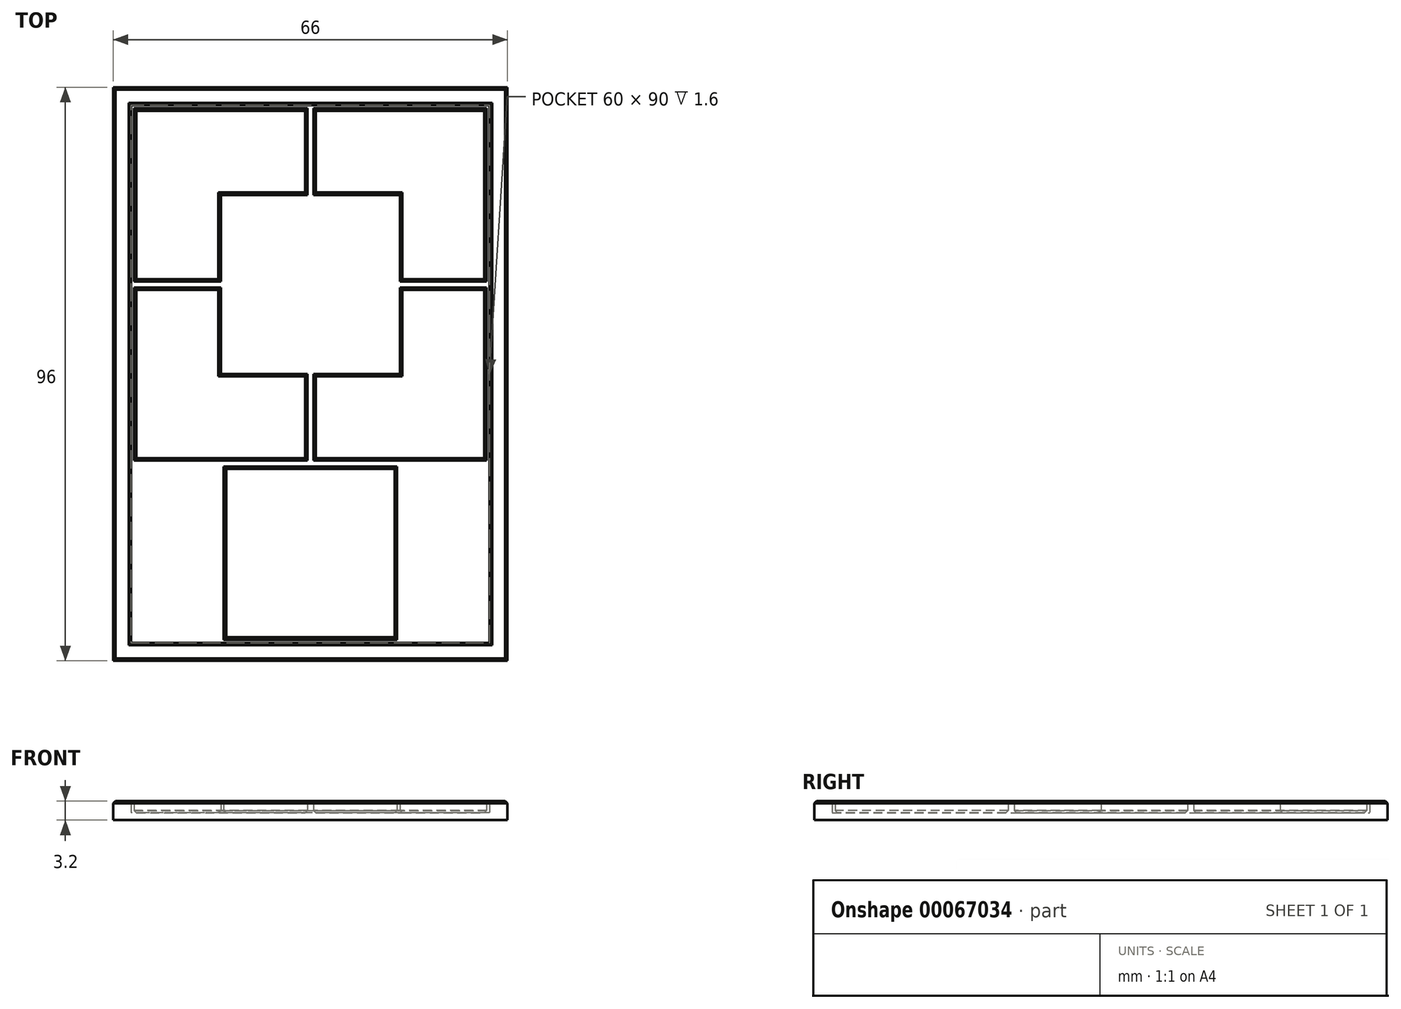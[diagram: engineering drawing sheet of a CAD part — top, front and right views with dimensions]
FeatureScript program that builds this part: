
annotation { "Feature Type Name" : "Feature", "Feature Type Description" : "" }
export const myFeature = defineFeature(function(context is Context, id is Id, definition is map)
    precondition{}
    {
        {
            var Q0;
            Q0=qCreatedBy(makeId("Top.planeOp"),FACE);
            var sketch = newSketch(context, id + "F0", { "sketchPlane" : qUnion([Q0])});
            skLineSegment(sketch, "E0.rect.bottom", {"start": v(-30, 45) * mm, "end": v(30, 45) * mm});
            skLineSegment(sketch, "E0.rect.top", {"start": v(-30, -45) * mm, "end": v(30, -45) * mm});
            skLineSegment(sketch, "E0.rect.left", {"start": v(-30, 45) * mm, "end": v(-30, -45) * mm});
            skLineSegment(sketch, "E0.rect.right", {"start": v(30, 45) * mm, "end": v(30, -45) * mm});
            skPoint(sketch, "E0.rect.middle", {"position": v(0, 0) * mm});
            skLineSegment(sketch, "E1.0", {"start": v(-33, 48) * mm, "end": v(-33, -48) * mm});
            skLineSegment(sketch, "E1.1", {"start": v(-33, 48) * mm, "end": v(33, 48) * mm});
            skLineSegment(sketch, "E1.2", {"start": v(33, 48) * mm, "end": v(33, -48) * mm});
            skLineSegment(sketch, "E1.3", {"start": v(-33, -48) * mm, "end": v(33, -48) * mm});
            skSolve(sketch);
        }
        {
            var Q0;
            Q0 = qSketchRegion(id + "F0", true);
            var Q1;
            Q1=makeQuery(id+"F0.imprint","IMPRINT",FACE,{"disambiguationData":[TD([[makeQuery(id+"F0.imprint","IMPRINT",EDGE,{"derivedFrom":sQuery(id+"F0.wireOp",EDGE,"E0.rect.bottom")}),-1.0]])]});
            extrude(context, id + "F1", {"entities" : qUnion([Q0, Q1]), "depth" : 1.2 * mm});
        }
        {
            var Q0;
            Q0=makeQuery(id+"F0.imprint","IMPRINT",FACE,{"disambiguationData":[TD([[makeQuery(id+"F0.imprint","IMPRINT",EDGE,{"derivedFrom":sQuery(id+"F0.wireOp",EDGE,"E0.rect.bottom")}),1.0]])]});
            extrude(context, id + "F2", {"entities" : qUnion([Q0]), "operationType" : NewBodyOperationType.ADD, "depth" : (1.2 + 2) * mm});
        }
        {
            var Q0;
            Q0=makeQuery(id+"F1.opExtrude","CAP_FACE",FACE,{"disambiguationData":[OSD([sQuery(id+"F0.wireOp",EDGE,"E1.0"),sQuery(id+"F0.wireOp",EDGE,"E1.1"),sQuery(id+"F0.wireOp",EDGE,"E1.2"),sQuery(id+"F0.wireOp",EDGE,"E1.3")])],"isStart":false});
            var sketch = newSketch(context, id + "F3", { "sketchPlane" : qUnion([Q0])});
            skLineSegment(sketch, "E2.bottom", {"start": v(-29.5, 44.5) * mm, "end": v(-0.5, 44.5) * mm});
            skLineSegment(sketch, "E2.top", {"start": v(-29.5, 15.5) * mm, "end": v(-15, 15.5) * mm});
            skLineSegment(sketch, "E2.left", {"start": v(-29.5, 44.5) * mm, "end": v(-29.5, 15.5) * mm});
            skLineSegment(sketch, "E2.right", {"start": v(-0.5, 44.5) * mm, "end": v(-0.5, 30) * mm});
            skLineSegment(sketch, "E3", {"start": v(-0.5, 30) * mm, "end": v(-15, 30) * mm});
            skLineSegment(sketch, "E4", {"start": v(-15, 30) * mm, "end": v(-15, 15.5) * mm});
            skLineSegment(sketch, "E5.0", {"start": v(-30, 45) * mm, "end": v(-30, -45) * mm, "construction": true});
            skLineSegment(sketch, "E5.1", {"start": v(-30, 45) * mm, "end": v(30, 45) * mm, "construction": true});
            skLineSegment(sketch, "E5.2", {"start": v(30, 45) * mm, "end": v(30, -45) * mm, "construction": true});
            skLineSegment(sketch, "E5.3", {"start": v(-30, -45) * mm, "end": v(30, -45) * mm, "construction": true});
            skLineSegment(sketch, "E6.0", {"start": v(-29.5, 44.5) * mm, "end": v(-29.5, -44.5) * mm, "construction": true});
            skLineSegment(sketch, "E6.1", {"start": v(-29.5, 44.5) * mm, "end": v(29.5, 44.5) * mm, "construction": true});
            skLineSegment(sketch, "E6.2", {"start": v(29.5, 44.5) * mm, "end": v(29.5, -44.5) * mm, "construction": true});
            skLineSegment(sketch, "E6.3", {"start": v(-29.5, -44.5) * mm, "end": v(29.5, -44.5) * mm, "construction": true});
            skLineSegment(sketch, "E7", {"start": v(-27.64, 15) * mm, "end": v(26.14, 15) * mm, "construction": true});
            skLineSegment(sketch, "E8", {"start": v(-27.76, -15) * mm, "end": v(23, -15) * mm, "construction": true});
            skLineSegment(sketch, "E9", {"start": v(0, -31.54) * mm, "end": v(0, 35.9) * mm, "construction": true});
            skLineSegment(sketch, "E10.1.0", {"start": v(-29.5, -14.5) * mm, "end": v(-0.5, -14.5) * mm});
            skLineSegment(sketch, "E10.1.1", {"start": v(-29.5, -14.5) * mm, "end": v(-29.5, 14.5) * mm});
            skLineSegment(sketch, "E10.1.2", {"start": v(-29.5, 14.5) * mm, "end": v(-15, 14.5) * mm});
            skLineSegment(sketch, "E10.1.3", {"start": v(-15, 14.5) * mm, "end": v(-15, 0) * mm});
            skLineSegment(sketch, "E10.1.4", {"start": v(-15, 0) * mm, "end": v(-0.5, 0) * mm});
            skLineSegment(sketch, "E10.1.5", {"start": v(-0.5, -14.5) * mm, "end": v(-0.5, 0) * mm});
            skLineSegment(sketch, "E10.2.0", {"start": v(29.5, -14.5) * mm, "end": v(29.5, 14.5) * mm});
            skLineSegment(sketch, "E10.2.1", {"start": v(29.5, -14.5) * mm, "end": v(0.5, -14.5) * mm});
            skLineSegment(sketch, "E10.2.2", {"start": v(0.5, -14.5) * mm, "end": v(0.5, 0) * mm});
            skLineSegment(sketch, "E10.2.3", {"start": v(0.5, 0) * mm, "end": v(15, 0) * mm});
            skLineSegment(sketch, "E10.2.4", {"start": v(15, 0) * mm, "end": v(15, 14.5) * mm});
            skLineSegment(sketch, "E10.2.5", {"start": v(29.5, 14.5) * mm, "end": v(15, 14.5) * mm});
            skLineSegment(sketch, "E10.3.0", {"start": v(29.5, 44.5) * mm, "end": v(0.5, 44.5) * mm});
            skLineSegment(sketch, "E10.3.1", {"start": v(29.5, 44.5) * mm, "end": v(29.5, 15.5) * mm});
            skLineSegment(sketch, "E10.3.2", {"start": v(29.5, 15.5) * mm, "end": v(15, 15.5) * mm});
            skLineSegment(sketch, "E10.3.3", {"start": v(15, 15.5) * mm, "end": v(15, 30) * mm});
            skLineSegment(sketch, "E10.3.4", {"start": v(15, 30) * mm, "end": v(0.5, 30) * mm});
            skLineSegment(sketch, "E10.3.5", {"start": v(0.5, 44.5) * mm, "end": v(0.5, 30) * mm});
            skPoint(sketch, "E10.center", {"position": v(0, 15) * mm});
            skLineSegment(sketch, "E11.rect.bottom", {"start": v(-14.5, -44.5) * mm, "end": v(14.5, -44.5) * mm});
            skLineSegment(sketch, "E11.rect.top", {"start": v(-14.5, -15.5) * mm, "end": v(14.5, -15.5) * mm});
            skLineSegment(sketch, "E11.rect.left", {"start": v(-14.5, -44.5) * mm, "end": v(-14.5, -15.5) * mm});
            skLineSegment(sketch, "E11.rect.right", {"start": v(14.5, -44.5) * mm, "end": v(14.5, -15.5) * mm});
            skPoint(sketch, "E11.rect.middle", {"position": v(0, -30) * mm});
            skSolve(sketch);
        }
        {
            var Q0;
            Q0=makeQuery(id+"F3.imprint","IMPRINT",FACE,{"disambiguationData":[TD([[makeQuery(id+"F3.imprint","IMPRINT",EDGE,{"derivedFrom":sQuery(id+"F3.wireOp",EDGE,"E2.bottom")}),-1.0]])]});
            var Q1;
            Q1=makeQuery(id+"F3.imprint","IMPRINT",FACE,{"disambiguationData":[TD([[makeQuery(id+"F3.imprint","IMPRINT",EDGE,{"derivedFrom":sQuery(id+"F3.wireOp",EDGE,"E10.3.0")}),1.0]])]});
            var Q2;
            Q2=makeQuery(id+"F3.imprint","IMPRINT",FACE,{"disambiguationData":[TD([[makeQuery(id+"F3.imprint","IMPRINT",EDGE,{"derivedFrom":sQuery(id+"F3.wireOp",EDGE,"E10.1.0")}),1.0]])]});
            var Q3;
            Q3=makeQuery(id+"F3.imprint","IMPRINT",FACE,{"disambiguationData":[TD([[makeQuery(id+"F3.imprint","IMPRINT",EDGE,{"derivedFrom":sQuery(id+"F3.wireOp",EDGE,"E10.2.0")}),1.0]])]});
            var Q4;
            Q4=makeQuery(id+"F3.imprint","IMPRINT",FACE,{"disambiguationData":[TD([[makeQuery(id+"F3.imprint","IMPRINT",EDGE,{"derivedFrom":sQuery(id+"F3.wireOp",EDGE,"E11.rect.bottom")}),1.0]])]});
            var Q5;
            Q5=makeQuery(id+"F2.opExtrude","CAP_FACE",FACE,{"disambiguationData":[OSD([sQuery(id+"F0.wireOp",EDGE,"E0.rect.bottom"),sQuery(id+"F0.wireOp",EDGE,"E0.rect.top"),sQuery(id+"F0.wireOp",EDGE,"E0.rect.left"),sQuery(id+"F0.wireOp",EDGE,"E0.rect.right"),sQuery(id+"F0.wireOp",EDGE,"E1.0"),sQuery(id+"F0.wireOp",EDGE,"E1.1"),sQuery(id+"F0.wireOp",EDGE,"E1.2"),sQuery(id+"F0.wireOp",EDGE,"E1.3")])],"isStart":false});
            extrude(context, id + "F4", {"entities" : qUnion([Q0, Q1, Q2, Q3, Q4]), "endBoundEntityFace" : qUnion([Q5]), "depth" : 2 * mm});
        }
        {
            var Q0;
            Q0=makeQuery(id+"F4.opExtrude","CAP_FACE",FACE,{"disambiguationData":[OSD([sQuery(id+"F3.wireOp",EDGE,"E2.bottom"),sQuery(id+"F3.wireOp",EDGE,"E2.top"),sQuery(id+"F3.wireOp",EDGE,"E2.left"),sQuery(id+"F3.wireOp",EDGE,"E2.right"),sQuery(id+"F3.wireOp",EDGE,"E3"),sQuery(id+"F3.wireOp",EDGE,"E4")])],"isStart":false});
            var Q1;
            Q1=makeQuery(id+"F4.opExtrude","CAP_FACE",FACE,{"disambiguationData":[OSD([sQuery(id+"F3.wireOp",EDGE,"E10.3.0"),sQuery(id+"F3.wireOp",EDGE,"E10.3.1"),sQuery(id+"F3.wireOp",EDGE,"E10.3.2"),sQuery(id+"F3.wireOp",EDGE,"E10.3.3"),sQuery(id+"F3.wireOp",EDGE,"E10.3.4"),sQuery(id+"F3.wireOp",EDGE,"E10.3.5")])],"isStart":false});
            var Q2;
            Q2=makeQuery(id+"F4.opExtrude","CAP_FACE",FACE,{"disambiguationData":[OSD([sQuery(id+"F3.wireOp",EDGE,"E10.2.0"),sQuery(id+"F3.wireOp",EDGE,"E10.2.1"),sQuery(id+"F3.wireOp",EDGE,"E10.2.2"),sQuery(id+"F3.wireOp",EDGE,"E10.2.3"),sQuery(id+"F3.wireOp",EDGE,"E10.2.4"),sQuery(id+"F3.wireOp",EDGE,"E10.2.5")])],"isStart":false});
            var Q3;
            Q3=makeQuery(id+"F4.opExtrude","CAP_FACE",FACE,{"disambiguationData":[OSD([sQuery(id+"F3.wireOp",EDGE,"E10.1.0"),sQuery(id+"F3.wireOp",EDGE,"E10.1.1"),sQuery(id+"F3.wireOp",EDGE,"E10.1.2"),sQuery(id+"F3.wireOp",EDGE,"E10.1.3"),sQuery(id+"F3.wireOp",EDGE,"E10.1.4"),sQuery(id+"F3.wireOp",EDGE,"E10.1.5")])],"isStart":false});
            var Q4;
            Q4=makeQuery(id+"F4.opExtrude","CAP_FACE",FACE,{"disambiguationData":[OSD([sQuery(id+"F3.wireOp",EDGE,"E11.rect.bottom"),sQuery(id+"F3.wireOp",EDGE,"E11.rect.top"),sQuery(id+"F3.wireOp",EDGE,"E11.rect.left"),sQuery(id+"F3.wireOp",EDGE,"E11.rect.right")])],"isStart":false});
            var Q5;
            Q5=makeQuery(id+"F4.opExtrude","CAP_FACE",FACE,{"disambiguationData":[OSD([sQuery(id+"F3.wireOp",EDGE,"E2.bottom"),sQuery(id+"F3.wireOp",EDGE,"E2.top"),sQuery(id+"F3.wireOp",EDGE,"E2.left"),sQuery(id+"F3.wireOp",EDGE,"E2.right"),sQuery(id+"F3.wireOp",EDGE,"E3"),sQuery(id+"F3.wireOp",EDGE,"E4")])],"isStart":true});
            var Q6;
            Q6=makeQuery(id+"F4.opExtrude","CAP_FACE",FACE,{"disambiguationData":[OSD([sQuery(id+"F3.wireOp",EDGE,"E10.1.0"),sQuery(id+"F3.wireOp",EDGE,"E10.1.1"),sQuery(id+"F3.wireOp",EDGE,"E10.1.2"),sQuery(id+"F3.wireOp",EDGE,"E10.1.3"),sQuery(id+"F3.wireOp",EDGE,"E10.1.4"),sQuery(id+"F3.wireOp",EDGE,"E10.1.5")])],"isStart":true});
            var Q7;
            Q7=makeQuery(id+"F4.opExtrude","CAP_FACE",FACE,{"disambiguationData":[OSD([sQuery(id+"F3.wireOp",EDGE,"E11.rect.bottom"),sQuery(id+"F3.wireOp",EDGE,"E11.rect.top"),sQuery(id+"F3.wireOp",EDGE,"E11.rect.left"),sQuery(id+"F3.wireOp",EDGE,"E11.rect.right")])],"isStart":true});
            var Q8;
            Q8=makeQuery(id+"F4.opExtrude","CAP_FACE",FACE,{"disambiguationData":[OSD([sQuery(id+"F3.wireOp",EDGE,"E10.2.0"),sQuery(id+"F3.wireOp",EDGE,"E10.2.1"),sQuery(id+"F3.wireOp",EDGE,"E10.2.2"),sQuery(id+"F3.wireOp",EDGE,"E10.2.3"),sQuery(id+"F3.wireOp",EDGE,"E10.2.4"),sQuery(id+"F3.wireOp",EDGE,"E10.2.5")])],"isStart":true});
            var Q9;
            Q9=makeQuery(id+"F4.opExtrude","CAP_FACE",FACE,{"disambiguationData":[OSD([sQuery(id+"F3.wireOp",EDGE,"E10.3.0"),sQuery(id+"F3.wireOp",EDGE,"E10.3.1"),sQuery(id+"F3.wireOp",EDGE,"E10.3.2"),sQuery(id+"F3.wireOp",EDGE,"E10.3.3"),sQuery(id+"F3.wireOp",EDGE,"E10.3.4"),sQuery(id+"F3.wireOp",EDGE,"E10.3.5")])],"isStart":true});
            var Q10;
            Q10=makeQuery(id+"F2.opExtrude","CAP_FACE",FACE,{"disambiguationData":[OSD([sQuery(id+"F0.wireOp",EDGE,"E0.rect.bottom"),sQuery(id+"F0.wireOp",EDGE,"E0.rect.top"),sQuery(id+"F0.wireOp",EDGE,"E0.rect.left"),sQuery(id+"F0.wireOp",EDGE,"E0.rect.right"),sQuery(id+"F0.wireOp",EDGE,"E1.0"),sQuery(id+"F0.wireOp",EDGE,"E1.1"),sQuery(id+"F0.wireOp",EDGE,"E1.2"),sQuery(id+"F0.wireOp",EDGE,"E1.3")])],"isStart":false});
            chamfer(context, id + "F5", {"entities" : qUnion([Q0, Q1, Q2, Q3, Q4, Q5, Q6, Q7, Q8, Q9, Q10]), "width" : 0.4 * mm, "tangentPropagation" : true});
        }
    });
